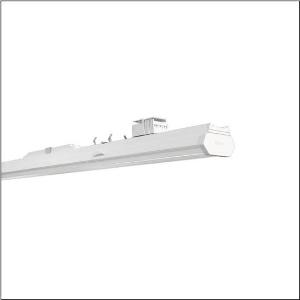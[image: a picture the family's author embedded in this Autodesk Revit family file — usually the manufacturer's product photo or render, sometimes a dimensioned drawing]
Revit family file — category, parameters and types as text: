
# Revit family: licross_11_protected_ho_51tp12dn4fxm
name_source: partatom
category: Lighting Fixtures
units: mm (PartAtom-declared; Revit-internal decimal feet)

## family parameters
Cut with Voids When Loaded = No
Host = Face
Light Source = No
Part Type = Normal
Room Calculation Point = No
Round Connector Dimension = Use Diameter
Shared = No

## types (1)
- --- (1 x LED, 15270 lm, 87.3 W, 4000K)
    Apparent Load = 87 VA
    CIE Flux Codes = 70 91 97 98 100
    Color Rendering = 80
    Color Temperature = 4000K
    Default Elevation = 1800 mm
    Description = Licross 11 Protected HO, luminaire insert, of sheet steel, galvanised, coil coated, white, length: 1.500mm, width: 90mm, height: 101mm, LED rated luminous flux: 15.270lm, light colour: 840, SDCM (Standard Deviation of Colour Matching)MacAdam ≤ 2 SDCM (initial), control gear: DALI 2, with plug, 5-pole, with phase selection, mains connection: 220..240V, AC, 50/60Hz, rated input power: 87W, internal wiring halogen-free, primary optical cover: cover, of PMMA, light emission: direct distribution, primary light characteristic: symmetric, protection rating (complete): IP64, insulation class (complete): insulation class I (protective earthing), certification: CE, ENEC, VDE, UKCA, protection symbol: D if used in an environment with conductive dust loads with corresponding accessories, impact resistance: IK06, permissible ambient temperature for indoor applications: -25..+30°C, corresponds to IFS (International Featured Standards) requirements for safety and quality in the food industry, reducing of maximum allowable ambient temperature of 5°C with ceiling mounting, LABS conformity tested according to VDMA 24364:2018-05, The light source and the operating device comply with the requirements of the Ecodesign Regulation (EU) 2019/2020 and are replaceable in accordance with this regulation, packaging unit: 1 piece
    Height = 92 mm
    Lamp = 1 x LED
    Lamp Light Flux = 15270 lm
    Lamp Power = 87.3 W
    Lamp count = 1
    Length = 1500 mm
    Luminous efficacy = 175 lm/W
    Manufacturer = Siteco
    ModVariant = No
    Model = 51TP12DN4FXM
    Mounting Place = Ceiling
    Mounting Type = Pendant
    Number of Poles = 1
    OnlyDefault = Yes
    Power Factor = 1
    Product Name = Licross 11 Protected HO
    Product group = luminaire insert | ceiling pendant
    ProductGroupID = 901
    Protection Class = Protection class I
    Protection Degree = IP 64
    RLX_Detail_Level = 1
    RLX_Emergency_Light_Flux = 0 lm
    RLX_Emergency_Type = 0
    RLX_Emergency_Type_DB = No
    RlxData = <blob elided: 24545 chars, md5=4a8d4efd>
    Socket = socket
    Standby Power = 0 W
    System Light Flux = 15270 lm
    System Power = 87 W
    Type Comments = factory setting: luminous flux: 100 % | dim-lin: 254 | 589 mA
    Type Image = l_1256148.jpg
    URL = http://relux.com
    VarID = @adj_031937
    Voltage = 0 V
    Weight = 0.00 kg
    Width = 88 mm

## geometry (parser evidence)
native form markers: Blend x4, Sweep x9
no freeform markers — native parametric forms only
